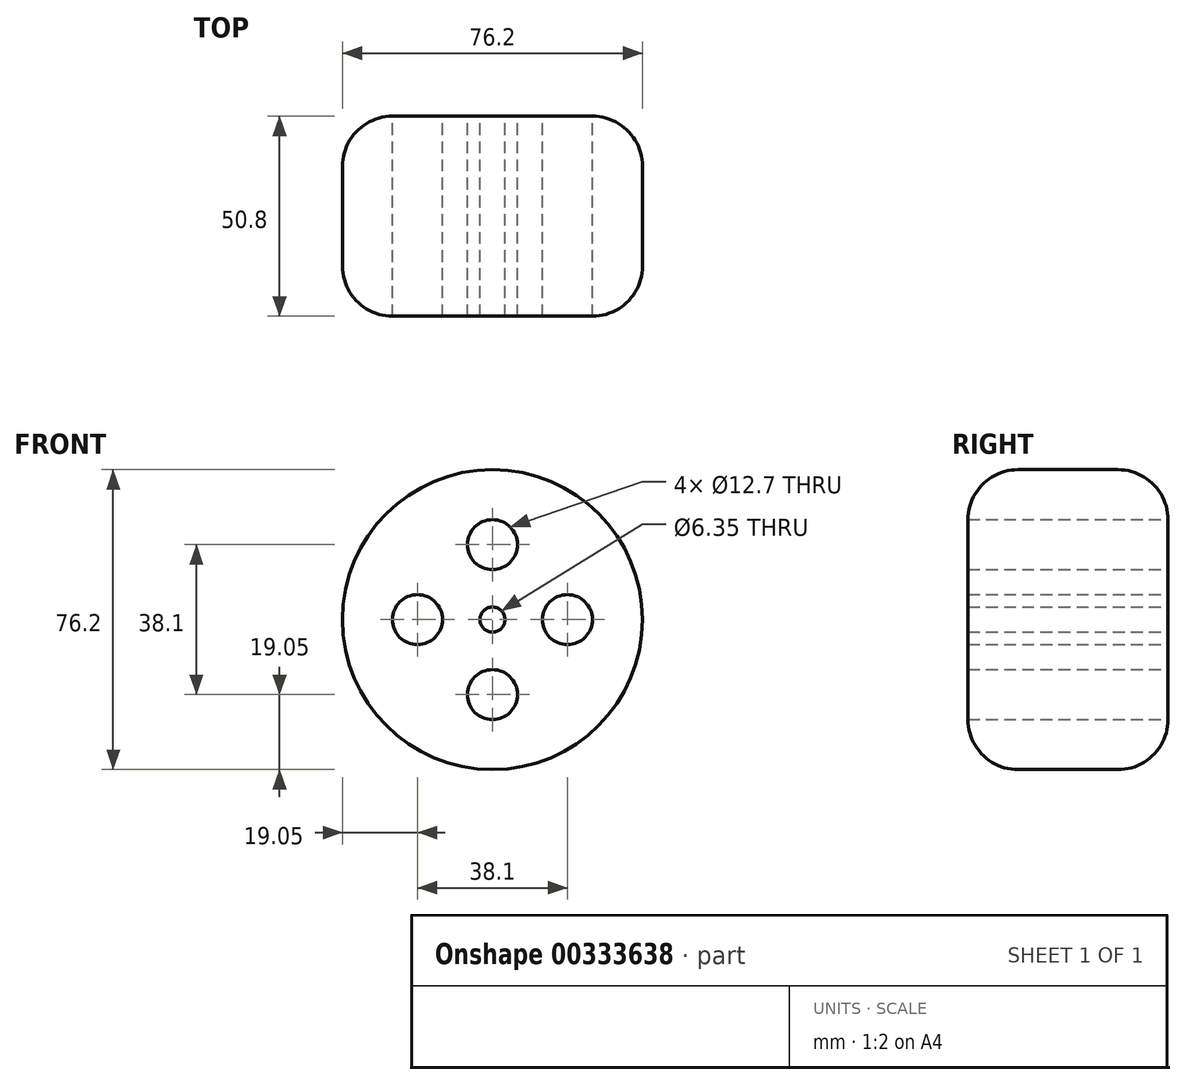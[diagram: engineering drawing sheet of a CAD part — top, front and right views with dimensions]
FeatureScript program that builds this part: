
annotation { "Feature Type Name" : "Feature", "Feature Type Description" : "" }
export const myFeature = defineFeature(function(context is Context, id is Id, definition is map)
    precondition{}
    {
        {
            var Q0;
            Q0=qCreatedBy(makeId("Front.planeOp"),FACE);
            var sketch = newSketch(context, id + "F0", { "sketchPlane" : qUnion([Q0])});
            skCircle(sketch, "E0", {"center": v(0, 0) * mm, "radius": 38.1 * mm});
            skCircle(sketch, "E1", {"center": v(-19.05, 0) * mm, "radius": 6.35 * mm});
            skCircle(sketch, "E2", {"center": v(0, 19.05) * mm, "radius": 6.35 * mm});
            skCircle(sketch, "E3", {"center": v(19.05, 0) * mm, "radius": 6.35 * mm});
            skCircle(sketch, "E4", {"center": v(0, -19.05) * mm, "radius": 6.35 * mm});
            skCircle(sketch, "E5", {"center": v(0, 0) * mm, "radius": 3.18 * mm});
            skSolve(sketch);
        }
        {
            var Q0;
            Q0=makeQuery(id+"F0.imprint","IMPRINT",FACE,{"disambiguationData":[TD([[makeQuery(id+"F0.imprint","IMPRINT",EDGE,{"derivedFrom":sQuery(id+"F0.wireOp",EDGE,"E0")}),1.0]])]});
            extrude(context, id + "F1", {"entities" : qUnion([Q0]), "depth" : 50.8 * mm});
        }
        {
            var Q0;
            Q0=makeQuery(id+"F1.opExtrude","CAP_EDGE",EDGE,{"disambiguationData":[OSD([sQuery(id+"F0.wireOp",EDGE,"E0")])],"isStart":false});
            fillet(context, id + "F2", {"entities" : qUnion([Q0]), "radius" : 12.7 * mm, "tangentPropagation" : true, "allowEdgeOverflow" : false});
        }
        {
            var Q0;
            Q0=makeQuery(id+"F1.opExtrude","CAP_EDGE",EDGE,{"disambiguationData":[OSD([sQuery(id+"F0.wireOp",EDGE,"E0")])],"isStart":true});
            fillet(context, id + "F3", {"entities" : qUnion([Q0]), "radius" : 12.7 * mm, "tangentPropagation" : true, "allowEdgeOverflow" : false});
        }
    });
